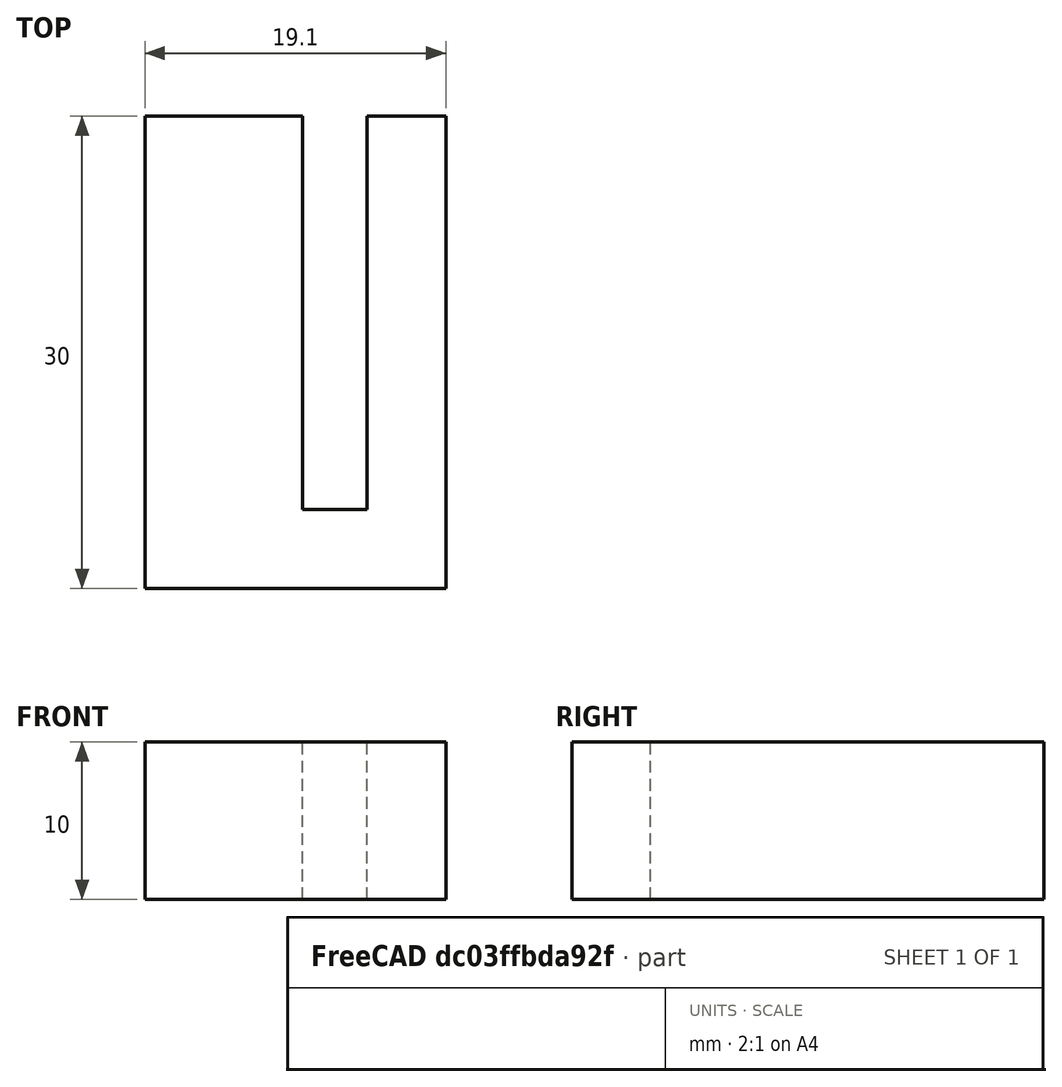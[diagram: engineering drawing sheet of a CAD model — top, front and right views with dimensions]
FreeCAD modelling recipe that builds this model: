
FCSTD DOCUMENT  (FreeCAD 0.20R29177 +426 (Git))
Label: grillWastePipeHolder
License: All rights reserved
LicenseURL: http://en.wikipedia.org/wiki/All_rights_reserved
objects: Sketcher::SketchObject×1, Spreadsheet::Sheet×1, PartDesign::Pad×1, PartDesign::Body×1
note: 4 computed .brp shape members not serialized (recipe doc carries the construction recipe); baked Part::Feature solids carry a one-line shape summary decoded from their .brp

FEATURE [Sketcher::SketchObject] Sketch
  FullyConstrained = true
  MapMode = 5
  Support = -> [XY_Plane]
  expr: Constraints[10] = Spreadsheet.holderToHole
  expr: Constraints[11] = Spreadsheet.totalRodDiameter
  expr: Constraints[12] = Spreadsheet.holderAwayFromHole
  expr: Constraints[20] = Spreadsheet.holderDepth
  expr: Constraints[21] = Spreadsheet.holderDepth
  expr: Constraints[22] = Spreadsheet.holderBackThickness
  sketch-geometry (8):
    g0: LineSegment StartX=0 StartY=30 StartZ=0 EndX=10 EndY=30 EndZ=0
    g1: LineSegment StartX=0 StartY=0 StartZ=0 EndX=0 EndY=30 EndZ=0
    g2: LineSegment StartX=14.1 StartY=30 StartZ=0 EndX=19.1 EndY=30 EndZ=0
    g3: LineSegment StartX=19.1 StartY=30 StartZ=0 EndX=19.1 EndY=0 EndZ=0
    g4: LineSegment StartX=14.1 StartY=5 StartZ=0 EndX=14.1 EndY=30 EndZ=0
    g5: LineSegment StartX=10 StartY=5 StartZ=0 EndX=14.1 EndY=5 EndZ=0
    g6: LineSegment StartX=10 StartY=30 StartZ=0 EndX=10 EndY=5 EndZ=0
    g7: LineSegment StartX=0 StartY=0 StartZ=0 EndX=19.1 EndY=0 EndZ=0
  constraints (23):
    c: Coincident(g0,g6)
    c: Coincident(g1,g0)
    c: Coincident(g2,g3)
    c: Coincident(g4,g2)
    c: Horizontal(g2)
    c: PointOnObject(g3,g-1)
    c: Horizontal(g5)
    c: Coincident(g6,g5)
    c: Coincident(g7,g1)
    c: Coincident(g3,g7)
    c: DistanceX(g0,g0) = 10
    c: DistanceX(g5,g5) = 4.1
    c: DistanceX(g2,g2) = 5
    c: Coincident(g4,g5)
    c: Vertical(g4)
    c: Vertical(g6)
    c: Vertical(g3)
    c: PointOnObject(g0,g-2)
    c: Coincident(g1,g-1)
    c: Horizontal(g0)
    c: DistanceY(g1,g1) = 30
    c: DistanceY(g3,g3) = 30
    c: DistanceY(g1,g5) = 5
FEATURE [Spreadsheet::Sheet] Spreadsheet
  cells = A2=rodDia; B2=4; A3=rodSpacing; B3=0.1; A4=totalRodDiameter; B4(totalRodDiameter)==B2 + B3; A5=holderDepth; B5(holderDepth)=30; A6=holderHeight; B6(holderHeight)=10; C6=should be 30; A7=holderToHole; B7(holderToHole)=10; A8=holderAwayFromHole; B8(holderAwayFromHole)=5; A9=holderBackThickness; B9(holderBackThickness)=5
FEATURE [PartDesign::Pad] Pad
  Direction = (0,0,1)
  Length = 10
  Length2 = 10
  Profile = -> Sketch
  ReferenceAxis = -> Sketch [N_Axis]
  Type = 0
  expr: Length = Spreadsheet.holderHeight
FEATURE [PartDesign::Body] Body
  Group = -> [Sketch,Pad]
  Origin = -> Origin
  Tip = -> Pad
